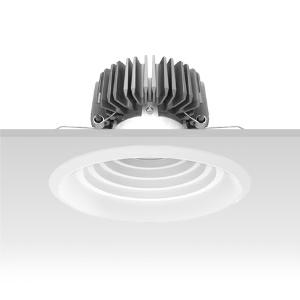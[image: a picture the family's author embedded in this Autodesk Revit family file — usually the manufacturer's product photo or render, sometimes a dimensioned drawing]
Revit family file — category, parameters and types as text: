
# Revit family: 3f_filippi_-_3f_reno_bianco_ellittico_3f_filippi_-_30793_-_3f_reno_200_wh_3000-840_ell
name_source: partatom
category: Lighting Fixtures
units: mm (PartAtom-declared; Revit-internal decimal feet)

## family parameters
Cut with Voids When Loaded = No
Host = Face
Light Source = No
Part Type = Normal
Room Calculation Point = No
Round Connector Dimension = Use Diameter
Shared = No

## types (1)
- 3F Filippi - 3F Reno Bianco Ellittico (1 x LED, 2810 lm, 28 W, 4000 K)
    Apparent Load = 28 VA
    Approval mark = CE
    CIE Flux Codes = 77 98 100 100 100
    Color Rendering = 80
    Color Temperature = 4000 K
    Control Gear = Electronic ballast
    Default Elevation = 1800 mm
    Description = ILLUMINOTECHNICAL
Luminous efficiency 100% (DLOR 100%, ULOR 0%).
Initial luminous flux of the luminaire 2810 lm.
Direct symmetric elliptical distribution.
Installation Interdistance Transv.D = 0.79 x hu - Long.D = 1.49 x hu.
Tabular UGR (CIE 117 - 4H-8H; S=0.25H; 70/50/20): RUG 18.3 - 22.8.
Beam angle: 65° - 93°.
Luminous efficacy 100 lm/W.
Lifetime (L90/B10): 30000 h. (tq+25°C)
Lifetime (L85/B10): 50000 h. (tq+25°C)
Lifetime (L70/B10): 80000 h. (tq+25°C)
Sudden decreased luminous flux after 50000 hours: 0% (C0).
Photobiological safety in compliance with IEC/TR 62778: RG1 low risk, (IEC 62471).
In compliance with IEC/EN 62722-2-1 - IEC/EN 62717 standards.

SOURCE
Compact LED module 3000/840.
Energy efficiency class (UE 2019/2020 - UE 2019/2015): D.
CIE 13.3 Colour rendering index: CRI >80 (R9 <50%).
IES TM-30 Fidelity Index: Rf = 84 Rg = 95.
CCT nominal colour temperature 4000 K.
Colour initial tolerance (MacAdam): SDCM 3.
Zhaga Book 3 compliant.

MECHANICAL
Passive heat dissipator in die-casting aluminium, oversized, for optimum thermal management of the LED module.
Parabolic element with graduated/concentric rings in white polycarbonate.
Internal specular metallic louvre to optimise control of the luminous flux in polycarbonate.
Transparent external lens with glossy and satin differentiated surfaces, with a cooling and anti-insect system in methacrylate (PMMA).
Fastening spring clips in stainless steel.
Dimensions: diameter 216 mm, height 142 mm. Weight 1.34 kg.
IP44 protection degree for exposed part, IP20 for recessed part.
Mechanical strength to impacts IK04 (0.5 joule).
Glow-wire test resistance 650°C.

ELECTRICAL
Wiring on a separate unit.
Halogen Free electronic wiring 230V-50/60Hz, power factor 0.95, THD <25%, constant output current, SELV, class II, 1 driver.
Power of the luminaire 28 W.
ENEC - CE.
SAFE FLICKER: PstLM=<1 and SVM=<0.4 (IEC TR 61547-1 and IEC TR 63158), to ensure a more comfortable and safe light.
Luminaire compliant with EN 60598-2-22 for power supply from a centralised emergency system CPSS (Central Power Supply System), not incorporated in the luminaire - high risk areas excluded. The default power and flux are 100% in AC and 100% in DC.
Ambient temperature from 0°C to +25°C.
Temperature class T6 max 85°C.
Relative humidity UR: <85%.

INSTALLATION
Pull-up recessed fitting.
False ceiling carving: 200 mm.
All accessories dedicated to this product are available on the Catalog and on our website www.3F-Filippi.com.

APPLICATIONS
Environments: architectural, commercial, exhibition areas, transit areas, corridors, shops, display windows, service areas.
In false ceilings with narrow voids.

WARNING
Luminaire designed for disposal/recycling at end-of-life.
Replaceable (LED only) light source by a professional. Replaceable control gear by a professional.
    Height = 0 mm  [stored 0 ft]
    Lamp = 1 x LED
    Lamp Light Flux = 2810 lm
    Lamp Power = 28 W
    Lamp count = 1
    Length = 216 mm
    Lifetime = 50000 h
    Luminous efficacy = 100 lm/W
    Manufacturer = 3F Filippi
    ModVariant = No
    Model = 3F Filippi - 30793 - 3F Reno 200 WH 3000-840 ELL
    Mounting Place = Ceiling
    Mounting Type = Recessed
    Number of Poles = 1
    OnlyDefault = Yes
    Power Factor = 1
    Product Name = 3F Filippi - 3F Reno Bianco Ellittico
    Product group = recessed luminaire
    ProductGroupID = 4
    Protection Class = Protection class II
    Protection Degree = IP 20
    RLX_Detail_Level = 1
    RLX_Emergency_Light_Flux = 0 lm
    RLX_Emergency_Type = 0
    RLX_Emergency_Type_DB = No
    RlxData = <blob elided: 94037 chars, md5=975db0cf>
    Socket = socket
    Standby Power = 0 W
    System Light Flux = 2810 lm
    System Power = 28 W
    Type Comments = Product without accessories
    Type Image = 3ffilippi_3f_reno_200_wh_2500_3000_4000.jpg
    URL = http://relux.com
    VarID = ---
    Voltage = 0 V
    Weight = 0.00 kg
    Width = 0 mm  [stored 0 ft]

note: [stored X ft] marks values corroborated as IEEE doubles in the binary element streams (Revit-internal decimal feet)

## geometry (parser evidence)
native form markers: Blend x4, Sweep x11
no freeform markers — native parametric forms only
